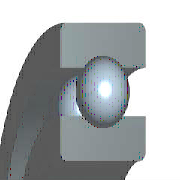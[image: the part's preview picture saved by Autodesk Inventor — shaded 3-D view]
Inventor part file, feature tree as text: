
AUTODESK INVENTOR PART (.ipt)
format: ipt  version: 2015 (Build 190159000, 159)  size: 345,088 bytes
history: native  units: mm (DEFAULTED — no unit token found)
features: sketch x5, other x3, plane x2, pattern_circular x1, fillet x1
ambient origin geometry x8: Origin, YZ Plane, XZ Plane, XY Plane, X Axis, Y Axis, Z Axis, Center Point
bodies: Solid1 (feature_tree)
feature tree (12):
  sketch  "Sketch1"  dims[d2=72.0mm]
  other  "WorkPoint1"
  other  "WorkAxis1"
  plane  "WorkPlane3"
  plane  "WorkPlane4"
  sketch  "Sketch4"  dims[d5=4.0mm]
  other  "WorkPoint2"
  pattern_circular  "PolarArray1"  Count=2  [1 undecoded]
  fillet  "Fillet1"  Radius=3.0mm
  sketch  "Sketch2"  dims[d3=10.0mm]
  sketch  "Sketch3"  dims[d4=19.0mm]
  sketch  "Sketch5"  dims[d6=360.0deg d7=0.0mm d8=15.6mm d9=2.1mm d10=360.0deg d11=-4.0mm d12=0.0mm d13=0.0mm d14=15.6001mm d15=2.1001mm d16=360.0deg d17=50.428571mm d19=360.0deg d20=0.15mm d21=2.62mm d22=3.25mm d23=3.88mm d26=0.0mm d27=0.0mm d28=0.0mm d29=0.0mm d30=0.0mm]
note: 1 required parameter value undecoded (feature->parameter linkage not recoverable at this tier; creation-order binding heuristic only, values carry confidence <= 0.55)
